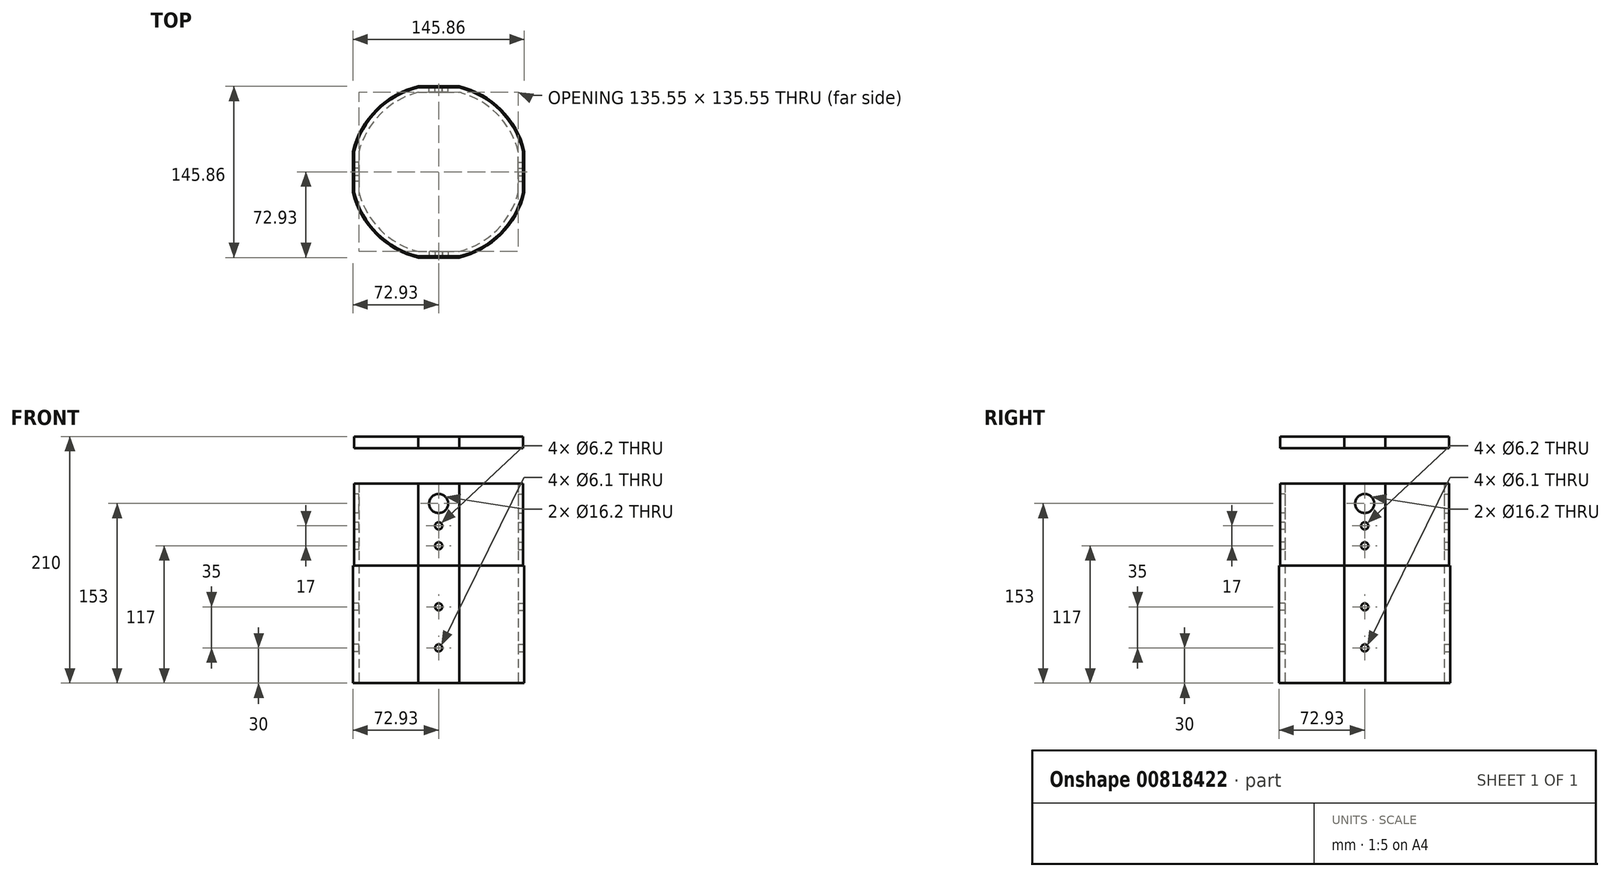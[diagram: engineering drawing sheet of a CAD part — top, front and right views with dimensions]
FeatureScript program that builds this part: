
annotation { "Feature Type Name" : "Feature", "Feature Type Description" : "" }
export const myFeature = defineFeature(function(context is Context, id is Id, definition is map)
    precondition{}
    {
        {
            var Q0;
            Q0=qCreatedBy(makeId("Top.planeOp"),FACE);
            var sketch = newSketch(context, id + "F0", { "sketchPlane" : qUnion([Q0])});
            skArc(sketch, "E0", {"start": v(-17.5, 72.93) * mm, "mid": v(-53.03, 53.03) * mm, "end": v(-72.93, 17.5) * mm});
            skArc(sketch, "E1", {"start": v(-72.93, -17.5) * mm, "mid": v(-53.03, -53.03) * mm, "end": v(-17.5, -72.93) * mm});
            skArc(sketch, "E2", {"start": v(17.5, -72.93) * mm, "mid": v(53.03, -53.03) * mm, "end": v(72.93, -17.5) * mm});
            skArc(sketch, "E3", {"start": v(72.93, 17.5) * mm, "mid": v(53.03, 53.03) * mm, "end": v(17.5, 72.93) * mm});
            skLineSegment(sketch, "E4", {"start": v(-72.93, 17.5) * mm, "end": v(-72.93, -17.5) * mm});
            skLineSegment(sketch, "E5", {"start": v(-17.5, 72.93) * mm, "end": v(17.5, 72.93) * mm});
            skLineSegment(sketch, "E6", {"start": v(72.93, 17.5) * mm, "end": v(72.93, -17.5) * mm});
            skLineSegment(sketch, "E7", {"start": v(-17.5, -72.93) * mm, "end": v(17.5, -72.93) * mm});
            skArc(sketch, "E8", {"start": v(-17.5, 67.78) * mm, "mid": v(-49.5, 49.5) * mm, "end": v(-67.78, 17.5) * mm});
            skArc(sketch, "E9", {"start": v(-67.78, -17.5) * mm, "mid": v(-49.5, -49.5) * mm, "end": v(-17.5, -67.78) * mm});
            skArc(sketch, "E10", {"start": v(17.5, -67.78) * mm, "mid": v(49.5, -49.5) * mm, "end": v(67.78, -17.5) * mm});
            skArc(sketch, "E11", {"start": v(67.78, 17.5) * mm, "mid": v(49.5, 49.5) * mm, "end": v(17.5, 67.78) * mm});
            skLineSegment(sketch, "E12", {"start": v(-17.5, 67.78) * mm, "end": v(17.5, 67.78) * mm});
            skLineSegment(sketch, "E13", {"start": v(-67.78, 17.5) * mm, "end": v(-67.78, -17.5) * mm});
            skLineSegment(sketch, "E14", {"start": v(-17.5, -67.78) * mm, "end": v(17.5, -67.78) * mm});
            skLineSegment(sketch, "E15", {"start": v(67.78, -17.5) * mm, "end": v(67.78, 17.5) * mm});
            skSolve(sketch);
        }
        {
            var Q0;
            Q0=qSketchRegion(id+"F0",true);
            extrude(context, id + "F1", {"entities" : qUnion([Q0]), "depth" : 100 * mm, "offsetDistance" : 25 * mm});
        }
        {
            var Q0;
            Q0=makeQuery(id+"F1.opExtrude","CAP_FACE",FACE,{"disambiguationData":[OSD([sQuery(id+"F0.wireOp",EDGE,"E0"),sQuery(id+"F0.wireOp",EDGE,"E1"),sQuery(id+"F0.wireOp",EDGE,"E2"),sQuery(id+"F0.wireOp",EDGE,"E3"),sQuery(id+"F0.wireOp",EDGE,"E4"),sQuery(id+"F0.wireOp",EDGE,"E5"),sQuery(id+"F0.wireOp",EDGE,"E6"),sQuery(id+"F0.wireOp",EDGE,"E7"),sQuery(id+"F0.wireOp",EDGE,"E8"),sQuery(id+"F0.wireOp",EDGE,"E9"),sQuery(id+"F0.wireOp",EDGE,"E10"),sQuery(id+"F0.wireOp",EDGE,"E11"),sQuery(id+"F0.wireOp",EDGE,"E12"),sQuery(id+"F0.wireOp",EDGE,"E13"),sQuery(id+"F0.wireOp",EDGE,"E14"),sQuery(id+"F0.wireOp",EDGE,"E15")])],"isStart":false});
            var sketch = newSketch(context, id + "F2", { "sketchPlane" : qUnion([Q0])});
            skArc(sketch, "E16.0", {"start": v(-17.5, 67.78) * mm, "mid": v(-49.5, 49.5) * mm, "end": v(-67.78, 17.5) * mm});
            skLineSegment(sketch, "E16.1", {"start": v(-67.78, 17.5) * mm, "end": v(-67.78, -17.5) * mm});
            skArc(sketch, "E16.2", {"start": v(-67.78, -17.5) * mm, "mid": v(-49.5, -49.5) * mm, "end": v(-17.5, -67.78) * mm});
            skLineSegment(sketch, "E16.3", {"start": v(-17.5, -67.78) * mm, "end": v(17.5, -67.78) * mm});
            skArc(sketch, "E16.4", {"start": v(17.5, -67.78) * mm, "mid": v(49.5, -49.5) * mm, "end": v(67.78, -17.5) * mm});
            skLineSegment(sketch, "E16.5", {"start": v(67.78, -17.5) * mm, "end": v(67.78, 17.5) * mm});
            skArc(sketch, "E16.6", {"start": v(67.78, 17.5) * mm, "mid": v(49.5, 49.5) * mm, "end": v(17.5, 67.78) * mm});
            skLineSegment(sketch, "E16.7", {"start": v(-17.5, 67.78) * mm, "end": v(17.5, 67.78) * mm});
            skArc(sketch, "E17", {"start": v(-17.5, 71.9) * mm, "mid": v(-52.33, 52.33) * mm, "end": v(-71.9, 17.5) * mm});
            skArc(sketch, "E18", {"start": v(71.9, 17.5) * mm, "mid": v(52.33, 52.33) * mm, "end": v(17.5, 71.9) * mm});
            skLineSegment(sketch, "E19", {"start": v(-71.9, 17.5) * mm, "end": v(-71.9, -17.5) * mm});
            skLineSegment(sketch, "E20", {"start": v(-17.5, 71.9) * mm, "end": v(17.5, 71.9) * mm});
            skPoint(sketch, "E21.start.orphan", {"position": v(26, -67.78) * mm});
            skLineSegment(sketch, "E22", {"start": v(71.9, 17.5) * mm, "end": v(71.9, -17.5) * mm});
            skArc(sketch, "E23", {"start": v(-71.9, -17.5) * mm, "mid": v(-52.33, -52.33) * mm, "end": v(-17.5, -71.9) * mm});
            skArc(sketch, "E24", {"start": v(71.9, -17.5) * mm, "mid": v(52.33, -52.33) * mm, "end": v(17.5, -71.9) * mm});
            skLineSegment(sketch, "E25", {"start": v(-17.5, -71.9) * mm, "end": v(17.5, -71.9) * mm});
            skSolve(sketch);
        }
        {
            var Q0;
            Q0=qSketchRegion(id+"F2",true);
            extrude(context, id + "F3", {"entities" : qUnion([Q0]), "operationType" : NewBodyOperationType.ADD, "depth" : 70 * mm, "offsetDistance" : 25 * mm});
        }
        {
            var Q0;
            Q0=makeQuery(id+"F3.opExtrude","SWEPT_FACE",FACE,{"disambiguationData":[OSD([sQuery(id+"F2.wireOp",EDGE,"E25")])]});
            var sketch = newSketch(context, id + "F4", { "sketchPlane" : qUnion([Q0])});
            skCircle(sketch, "E26", {"center": v(0, 153) * mm, "radius": 8.1 * mm});
            skCircle(sketch, "E27", {"center": v(0, 134) * mm, "radius": 3.1 * mm});
            skCircle(sketch, "E28", {"center": v(0, 117) * mm, "radius": 3.1 * mm});
            skSolve(sketch);
        }
        {
            var Q0;
            Q0=qSketchRegion(id+"F4",true);
            var Q1;
            Q1=makeQuery(id+"F3.boolean.opBoolean","MERGE",FACE,{"derivedFrom":[makeQuery(id+"F1.opExtrude","SWEPT_FACE",FACE,{"disambiguationData":[OSD([sQuery(id+"F0.wireOp",EDGE,"E14")])]}),makeQuery(id+"F3.opExtrude","SWEPT_FACE",FACE,{"disambiguationData":[OSD([sQuery(id+"F2.wireOp",EDGE,"E16.3")])]})]});
            extrude(context, id + "F5", {"entities" : qUnion([Q0]), "operationType" : NewBodyOperationType.REMOVE, "endBound" : BoundingType.UP_TO_SURFACE, "oppositeDirection" : true, "depth" : 25 * mm, "endBoundEntityFace" : qUnion([Q1]), "offsetDistance" : 25 * mm});
        }
        {
            var Q0;
            Q0=makeQuery(id+"F3.opExtrude","SWEPT_FACE",FACE,{"disambiguationData":[OSD([sQuery(id+"F2.wireOp",EDGE,"E22")])]});
            var sketch = newSketch(context, id + "F6", { "sketchPlane" : qUnion([Q0])});
            skCircle(sketch, "E29", {"center": v(0, 153) * mm, "radius": 8.1 * mm});
            skCircle(sketch, "E30", {"center": v(0, 134) * mm, "radius": 3.1 * mm});
            skCircle(sketch, "E31", {"center": v(0, 117) * mm, "radius": 3.1 * mm});
            skSolve(sketch);
        }
        {
            var Q0;
            Q0=qSketchRegion(id+"F6",true);
            var Q1;
            Q1=makeQuery(id+"F3.boolean.opBoolean","MERGE",FACE,{"derivedFrom":[makeQuery(id+"F1.opExtrude","SWEPT_FACE",FACE,{"disambiguationData":[OSD([sQuery(id+"F0.wireOp",EDGE,"E15")])]}),makeQuery(id+"F3.opExtrude","SWEPT_FACE",FACE,{"disambiguationData":[OSD([sQuery(id+"F2.wireOp",EDGE,"E16.5")])]})]});
            extrude(context, id + "F7", {"entities" : qUnion([Q0]), "operationType" : NewBodyOperationType.REMOVE, "endBound" : BoundingType.UP_TO_SURFACE, "oppositeDirection" : true, "depth" : 25 * mm, "endBoundEntityFace" : qUnion([Q1]), "offsetDistance" : 25 * mm});
        }
        {
            var Q0;
            Q0=makeQuery(id+"F3.opExtrude","SWEPT_FACE",FACE,{"disambiguationData":[OSD([sQuery(id+"F2.wireOp",EDGE,"E20")])]});
            var sketch = newSketch(context, id + "F8", { "sketchPlane" : qUnion([Q0])});
            skCircle(sketch, "E32", {"center": v(0, 153) * mm, "radius": 8.1 * mm});
            skCircle(sketch, "E33", {"center": v(0, 134) * mm, "radius": 3.1 * mm});
            skCircle(sketch, "E34", {"center": v(0, 117) * mm, "radius": 3.1 * mm});
            skSolve(sketch);
        }
        {
            var Q0;
            Q0=qSketchRegion(id+"F8",true);
            var Q1;
            Q1=makeQuery(id+"F3.boolean.opBoolean","MERGE",FACE,{"derivedFrom":[makeQuery(id+"F1.opExtrude","SWEPT_FACE",FACE,{"disambiguationData":[OSD([sQuery(id+"F0.wireOp",EDGE,"E12")])]}),makeQuery(id+"F3.opExtrude","SWEPT_FACE",FACE,{"disambiguationData":[OSD([sQuery(id+"F2.wireOp",EDGE,"E16.7")])]})]});
            extrude(context, id + "F9", {"entities" : qUnion([Q0]), "operationType" : NewBodyOperationType.REMOVE, "endBound" : BoundingType.UP_TO_SURFACE, "oppositeDirection" : true, "depth" : 25 * mm, "endBoundEntityFace" : qUnion([Q1]), "offsetDistance" : 25 * mm});
        }
        {
            var Q0;
            Q0=makeQuery(id+"F3.opExtrude","SWEPT_FACE",FACE,{"disambiguationData":[OSD([sQuery(id+"F2.wireOp",EDGE,"E19")])]});
            var sketch = newSketch(context, id + "F10", { "sketchPlane" : qUnion([Q0])});
            skCircle(sketch, "E35", {"center": v(0, 153) * mm, "radius": 8.1 * mm});
            skCircle(sketch, "E36", {"center": v(0, 134) * mm, "radius": 3.1 * mm});
            skCircle(sketch, "E37", {"center": v(0, 117) * mm, "radius": 3.1 * mm});
            skSolve(sketch);
        }
        {
            var Q0;
            Q0=qSketchRegion(id+"F10",true);
            extrude(context, id + "F11", {"entities" : qUnion([Q0]), "operationType" : NewBodyOperationType.REMOVE, "endBound" : BoundingType.UP_TO_NEXT, "oppositeDirection" : true, "depth" : 25 * mm, "offsetDistance" : 25 * mm});
        }
        {
            var Q0;
            Q0=makeQuery(id+"F1.opExtrude","SWEPT_FACE",FACE,{"disambiguationData":[OSD([sQuery(id+"F0.wireOp",EDGE,"E6")])]});
            var sketch = newSketch(context, id + "F12", { "sketchPlane" : qUnion([Q0])});
            skCircle(sketch, "E38", {"center": v(0, 65) * mm, "radius": 3.05 * mm});
            skCircle(sketch, "E39", {"center": v(0, 30) * mm, "radius": 3.05 * mm});
            skSolve(sketch);
        }
        {
            var Q0;
            Q0=qSketchRegion(id+"F12",true);
            extrude(context, id + "F13", {"entities" : qUnion([Q0]), "operationType" : NewBodyOperationType.REMOVE, "endBound" : BoundingType.UP_TO_NEXT, "oppositeDirection" : true, "depth" : 25 * mm, "offsetDistance" : 25 * mm});
        }
        {
            var Q0;
            Q0=makeQuery(id+"F1.opExtrude","SWEPT_FACE",FACE,{"disambiguationData":[OSD([sQuery(id+"F0.wireOp",EDGE,"E7")])]});
            var sketch = newSketch(context, id + "F14", { "sketchPlane" : qUnion([Q0])});
            skCircle(sketch, "E40", {"center": v(0, 65) * mm, "radius": 3.05 * mm});
            skCircle(sketch, "E41", {"center": v(0, 30) * mm, "radius": 3.05 * mm});
            skSolve(sketch);
        }
        {
            var Q0;
            Q0=qSketchRegion(id+"F14",true);
            extrude(context, id + "F15", {"entities" : qUnion([Q0]), "operationType" : NewBodyOperationType.REMOVE, "endBound" : BoundingType.UP_TO_NEXT, "oppositeDirection" : true, "depth" : 25 * mm, "offsetDistance" : 25 * mm});
        }
        {
            var Q0;
            Q0=makeQuery(id+"F1.opExtrude","SWEPT_FACE",FACE,{"disambiguationData":[OSD([sQuery(id+"F0.wireOp",EDGE,"E5")])]});
            var sketch = newSketch(context, id + "F16", { "sketchPlane" : qUnion([Q0])});
            skCircle(sketch, "E42", {"center": v(0, 65) * mm, "radius": 3.05 * mm});
            skCircle(sketch, "E43", {"center": v(0, 30) * mm, "radius": 3.05 * mm});
            skSolve(sketch);
        }
        {
            var Q0;
            Q0=qSketchRegion(id+"F16",true);
            extrude(context, id + "F17", {"entities" : qUnion([Q0]), "operationType" : NewBodyOperationType.REMOVE, "endBound" : BoundingType.UP_TO_NEXT, "oppositeDirection" : true, "depth" : 25 * mm, "offsetDistance" : 25 * mm});
        }
        {
            var Q0;
            Q0=makeQuery(id+"F1.opExtrude","SWEPT_FACE",FACE,{"disambiguationData":[OSD([sQuery(id+"F0.wireOp",EDGE,"E4")])]});
            var sketch = newSketch(context, id + "F18", { "sketchPlane" : qUnion([Q0])});
            skCircle(sketch, "E44", {"center": v(0, 65) * mm, "radius": 3.05 * mm});
            skCircle(sketch, "E45", {"center": v(0, 30) * mm, "radius": 3.05 * mm});
            skSolve(sketch);
        }
        {
            var Q0;
            Q0=qSketchRegion(id+"F18",true);
            extrude(context, id + "F19", {"entities" : qUnion([Q0]), "operationType" : NewBodyOperationType.REMOVE, "endBound" : BoundingType.UP_TO_NEXT, "oppositeDirection" : true, "depth" : 25 * mm, "offsetDistance" : 25 * mm});
        }
        {
            var Q0;
            Q0 = qSketchRegion(id + "F2", true);
            var Q1;
            Q1=makeQuery(id+"F2.imprint","IMPRINT",FACE,{"disambiguationData":[TD([[makeQuery(id+"F2.imprint","IMPRINT",EDGE,{"derivedFrom":sQuery(id+"F2.wireOp",EDGE,"E16.0")}),1.0]])]});
            extrude(context, id + "F20", {"entities" : qUnion([Q0, Q1]), "depth" : 110 * mm, "offsetDistance" : 25 * mm, "hasSecondDirection" : true, "secondDirectionOppositeDirection" : false, "secondDirectionDepth" : 100 * mm});
        }
    });
